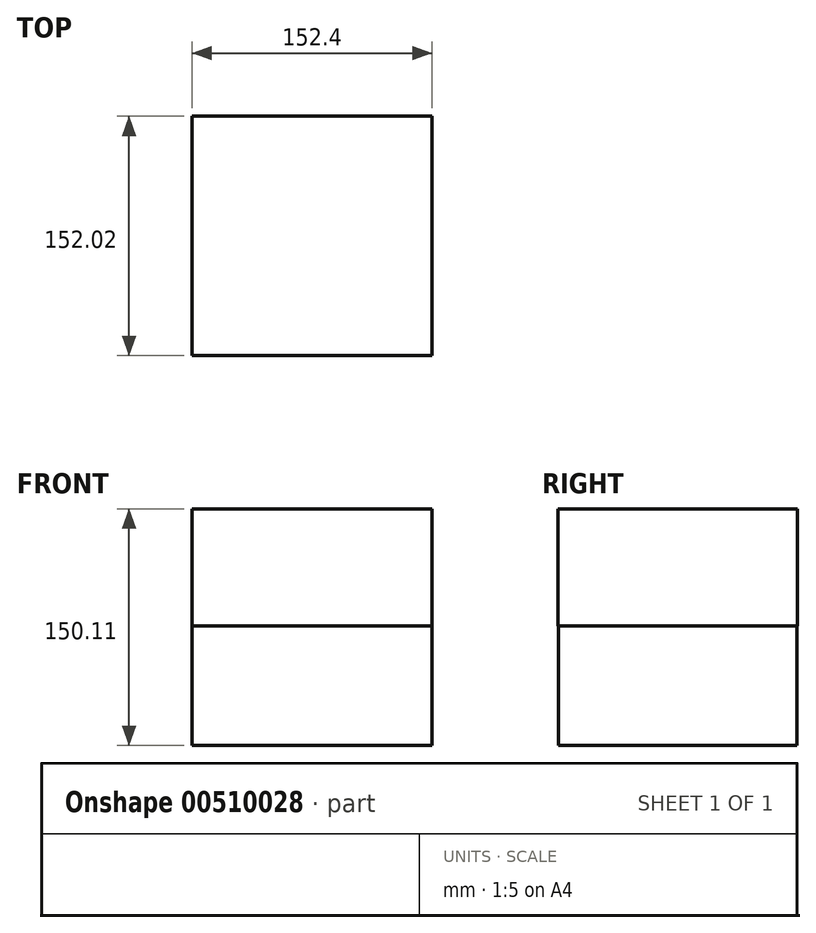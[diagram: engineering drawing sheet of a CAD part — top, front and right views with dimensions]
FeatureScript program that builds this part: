
annotation { "Feature Type Name" : "Feature", "Feature Type Description" : "" }
export const myFeature = defineFeature(function(context is Context, id is Id, definition is map)
    precondition{}
    {
        {
            var Q0;
            Q0=qCreatedBy(makeId("Top.planeOp"),FACE);
            var sketch = newSketch(context, id + "F0", { "sketchPlane" : qUnion([Q0])});
            skLineSegment(sketch, "E0.bottom", {"start": v(-76.15, 75.58) * mm, "end": v(76.12, 75.58) * mm});
            skLineSegment(sketch, "E0.top", {"start": v(-76.15, -75.8) * mm, "end": v(76.12, -75.8) * mm});
            skLineSegment(sketch, "E0.left", {"start": v(-76.15, 75.58) * mm, "end": v(-76.15, -75.8) * mm});
            skLineSegment(sketch, "E0.right", {"start": v(76.12, 75.58) * mm, "end": v(76.12, -75.8) * mm});
            skSolve(sketch);
        }
        {
            var Q0;
            Q0=makeQuery(id+"F0.imprint","IMPRINT",FACE,{"disambiguationData":[TD([[makeQuery(id+"F0.imprint","IMPRINT",EDGE,{"derivedFrom":sQuery(id+"F0.wireOp",EDGE,"E0.bottom")}),-1.0]])]});
            var sketch = newSketch(context, id + "F1", { "sketchPlane" : qUnion([Q0])});
            skLineSegment(sketch, "E1.bottom", {"start": v(-76.28, 75.92) * mm, "end": v(76.1, 75.92) * mm});
            skLineSegment(sketch, "E1.top", {"start": v(-76.28, -76.1) * mm, "end": v(76.1, -76.1) * mm});
            skLineSegment(sketch, "E1.left", {"start": v(-76.28, 75.92) * mm, "end": v(-76.28, -76.1) * mm});
            skLineSegment(sketch, "E1.right", {"start": v(76.1, 75.92) * mm, "end": v(76.1, -76.1) * mm});
            skSolve(sketch);
        }
        {
            var Q0;
            Q0 = qSketchRegion(id + "F1", true);
            extrude(context, id + "F2", {"entities" : qUnion([Q0]), "depth" : 74.42 * mm});
        }
        {
            var Q0;
            Q0=makeQuery(id+"F0.imprint","IMPRINT",FACE,{"disambiguationData":[TD([[makeQuery(id+"F0.imprint","IMPRINT",EDGE,{"derivedFrom":sQuery(id+"F0.wireOp",EDGE,"E0.bottom")}),-1.0]])]});
            extrude(context, id + "F3", {"entities" : qUnion([Q0]), "operationType" : NewBodyOperationType.ADD, "oppositeDirection" : true, "depth" : 75.7 * mm});
        }
    });
